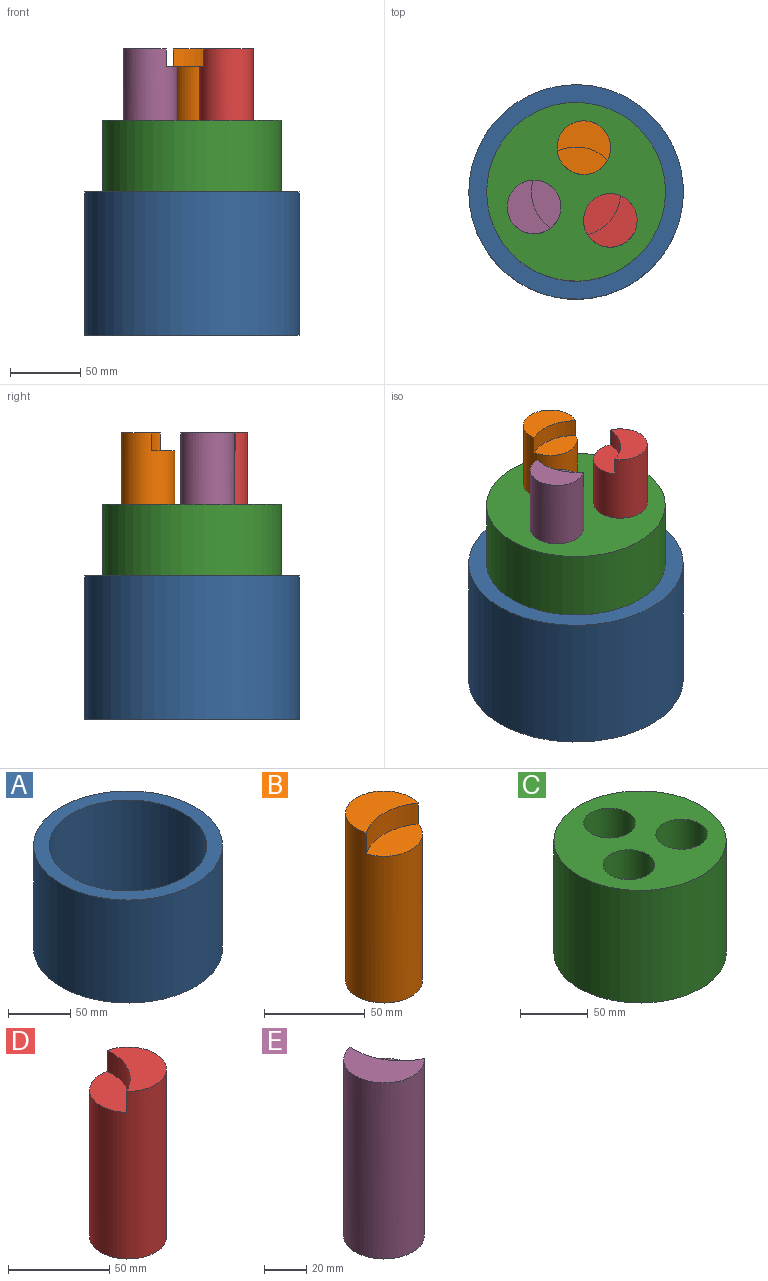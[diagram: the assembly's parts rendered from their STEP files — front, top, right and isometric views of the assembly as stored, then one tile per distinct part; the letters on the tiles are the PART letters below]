
ASSEMBLY  parts=5 mates=4
PART A: 4 faces, bbox 152.4x152.4x101.6 mm
  f0: cylinder r=63.5mm len=127mm, axis (0,0,-1), area 40536.6mm2, adj f2,f3
  f1: cylinder r=76.2mm len=152.4mm, axis (0,0,-1), area 48643.9mm2, adj f2,f3
  f2: plane 152.4x152.4mm, normal (0,0,1), area 5573.8mm2, adj f0,f1
  f3: plane 152.4x152.4mm, normal (0,0,-1), area 5573.8mm2, adj f0,f1
PART B: 5 faces, bbox 38.1x38.1x101.6 mm
  f0: cylinder r=19.05mm len=101.6mm, axis (0,0,-1), area 11548.3mm2, adj f1,f2,f3,f4
  f1: plane 38.1x24.77mm, normal (0,0,1), area 643.3mm2, adj f0,f4
  f2: plane 38.1x38.1mm, normal (0,0,-1), area 1140.1mm2, adj f0
  f3: plane 36.35x19.05mm, normal (0,0,1), area 496.8mm2, adj f0,f4
  f4: cylinder r=31.75mm len=36.35mm, axis (0,0,1), area 491.4mm2, adj f0,f1,f3
PART C: 6 faces, bbox 127x127x101.6 mm
  f0: cylinder r=63.5mm len=127mm, axis (0,0,-1), area 40536.6mm2, adj f1,f2
  f1: plane 127x127mm, normal (0,0,1), area 9247.4mm2, adj f0,f3,f4,f5
  f2: plane 127x127mm, normal (0,0,-1), area 9247.4mm2, adj f0,f3,f4,f5
  f3: cylinder r=19.05mm len=101.6mm, axis (0,0,1), area 12161mm2, adj f1,f2
  f4: cylinder r=19.05mm len=101.6mm, axis (0,0,1), area 12161mm2, adj f1,f2
  f5: cylinder r=19.05mm len=101.6mm, axis (0,0,1), area 12161mm2, adj f1,f2
PART D: 5 faces, bbox 38.1x38.1x101.6 mm
  f0: cylinder r=19.05mm len=101.6mm, axis (0,0,-1), area 11548.3mm2, adj f1,f2,f3,f4
  f1: plane 37.65x33.09mm, normal (0,0,1), area 643.3mm2, adj f0,f4
  f2: plane 38.1x38.1mm, normal (0,0,-1), area 1140.1mm2, adj f0
  f3: plane 31.93x23.3mm, normal (0,0,1), area 496.8mm2, adj f0,f4
  f4: cylinder r=31.75mm len=31.48mm, axis (0,0,1), area 491.4mm2, adj f0,f1,f3
PART E: 5 faces, bbox 38.1x38.1x101.6 mm
  f0: cylinder r=19.05mm len=101.6mm, axis (0,0,-1), area 11548.3mm2, adj f1,f2,f3,f4
  f1: plane 37.65x33.09mm, normal (0,0,1), area 643.3mm2, adj f0,f4
  f2: plane 38.1x38.1mm, normal (0,0,-1), area 1140.1mm2, adj f0
  f3: plane 31.93x23.3mm, normal (0,0,1), area 496.8mm2, adj f0,f4
  f4: cylinder r=31.75mm len=31.48mm, axis (0,0,1), area 491.4mm2, adj f0,f1,f3
PLACE A rot(axis=(0,0,-1),10deg) t=(-138.83,-9.71,-76.81)mm
PLACE B rot(axis=(0,0,-1),10deg) t=(-138.83,-9.71,-76.81)mm
PLACE C rot(axis=(0,0,-1),10deg) t=(-138.83,-9.71,-76.81)mm
PLACE D rot(axis=(0,0,-1),10deg) t=(-138.83,-9.71,-76.81)mm
PLACE E rot(axis=(0,0,-1),10deg) t=(-138.83,-9.71,-76.81)mm
MATE revolute B.f0 <-> C.f5  axis (0,0,-1) through (-133.32,21.55,24.79)mm
MATE revolute D.f0 <-> C.f4  axis (0,0,-1) through (-114.51,-30.12,24.79)mm
MATE revolute C.f0 <-> A.f0  axis (0,0,-1) through (-138.83,-9.71,-26.01)mm
MATE revolute E.f0 <-> C.f3  axis (0,0,-1) through (-168.67,-20.57,24.79)mm
